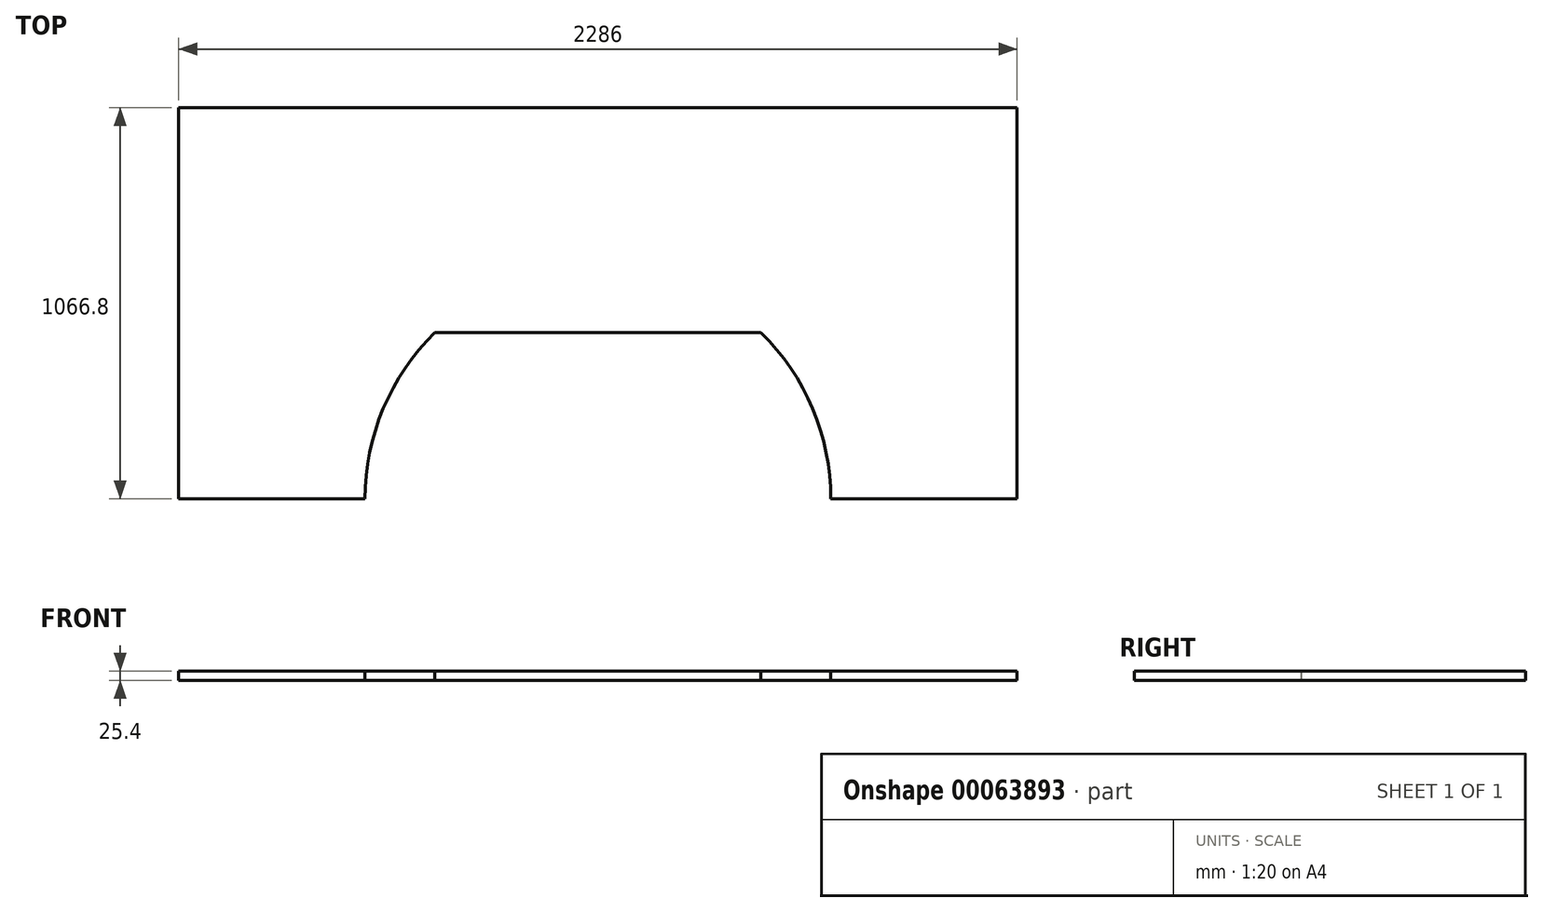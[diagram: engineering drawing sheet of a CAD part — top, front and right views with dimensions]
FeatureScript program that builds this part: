
annotation { "Feature Type Name" : "Feature", "Feature Type Description" : "" }
export const myFeature = defineFeature(function(context is Context, id is Id, definition is map)
    precondition{}
    {
        {
            var Q0;
            Q0=qCreatedBy(makeId("Top.planeOp"),FACE);
            var sketch = newSketch(context, id + "F0", { "sketchPlane" : qUnion([Q0])});
            skLineSegment(sketch, "E0.top", {"start": v(-1143, 609.6) * mm, "end": v(0, 609.6) * mm});
            skLineSegment(sketch, "E0.left", {"start": v(-1143, 0) * mm, "end": v(-1143, 609.6) * mm});
            skPoint(sketch, "E1.start.orphan", {"position": v(0, 177.8) * mm});
            skLineSegment(sketch, "E2", {"start": v(-1143, 0) * mm, "end": v(-1143, -457.2) * mm});
            skLineSegment(sketch, "E3", {"start": v(-1143, -457.2) * mm, "end": v(-635, -457.2) * mm});
            skLineSegment(sketch, "E4", {"start": v(-635, -457.2) * mm, "end": v(-635, -457.2) * mm});
            skArc(sketch, "E5", {"start": v(3.18, 177.8) * mm, "mid": v(0, 177.8) * mm, "end": v(-3.18, 177.8) * mm});
            skPoint(sketch, "E6.MirrorP", {"position": v(3.17, 177.64) * mm});
            skLineSegment(sketch, "E7.MirrorCS", {"start": v(634.96, -438.3) * mm, "end": v(634.96, -438.3) * mm});
            skLineSegment(sketch, "E8.MirrorCS", {"start": v(1135.13, -438.3) * mm, "end": v(1132.5, -438.3) * mm});
            skPoint(sketch, "E9.end.orphan", {"position": v(-585.44, -211.27) * mm});
            skPoint(sketch, "E10.orphan", {"position": v(-444.5, -3.72) * mm});
            skPoint(sketch, "E11.MirrorCS.end.orphan", {"position": v(0, 609.6) * mm});
            skLineSegment(sketch, "E12", {"start": v(0, 609.6) * mm, "end": v(0, -457.2) * mm, "construction": true});
            skLineSegment(sketch, "E13.MirrorCS", {"start": v(1143, 0) * mm, "end": v(1143, 609.6) * mm});
            skLineSegment(sketch, "E14.MirrorCS", {"start": v(1143, 0) * mm, "end": v(1143, -457.2) * mm});
            skLineSegment(sketch, "E15.MirrorCS", {"start": v(1143, -457.2) * mm, "end": v(635, -457.2) * mm});
            skArc(sketch, "E16.MirrorCS", {"start": v(-3.18, 177.8) * mm, "mid": v(0, 177.8) * mm, "end": v(3.18, 177.8) * mm});
            skPoint(sketch, "E17.MirrorP", {"position": v(-3.17, 177.64) * mm});
            skLineSegment(sketch, "E18.MirrorCS", {"start": v(1143, 609.6) * mm, "end": v(0, 609.6) * mm});
            skPoint(sketch, "E19.MirrorP", {"position": v(585.44, -211.27) * mm});
            skPoint(sketch, "E20.MirrorP", {"position": v(444.5, -3.72) * mm});
            skLineSegment(sketch, "E21", {"start": v(-444.5, -3.72) * mm, "end": v(444.5, -3.72) * mm});
            skArc(sketch, "E22.trimOffspring", {"start": v(-444.5, -3.72) * mm, "mid": v(-585.44, -211.27) * mm, "end": v(-635, -457.2) * mm});
            skArc(sketch, "E23.trimOffspring", {"start": v(444.5, -3.72) * mm, "mid": v(585.44, -211.27) * mm, "end": v(635, -457.2) * mm});
            skLineSegment(sketch, "E24", {"start": v(585.44, -211.27) * mm, "end": v(658.35, -177.84) * mm, "construction": true});
            skPoint(sketch, "E25.orphan", {"position": v(-658.35, -177.84) * mm});
            skSolve(sketch);
        }
        {
            var Q0;
            Q0=makeQuery(id+"F0.imprint","IMPRINT",FACE,{"disambiguationData":[TD([[makeQuery(id+"F0.imprint","IMPRINT",EDGE,{"derivedFrom":sQuery(id+"F0.wireOp",EDGE,"E0.top")}),-1.0]])]});
            extrude(context, id + "F1", {"entities" : qUnion([Q0]), "depth" : 25.4 * mm});
        }
        {
            var Q0;
            Q0 = qSketchRegion(id + "F0", true);
            extrude(context, id + "F2", {"entities" : qUnion([Q0]), "operationType" : NewBodyOperationType.ADD, "depth" : 25.4 * mm});
        }
    });
